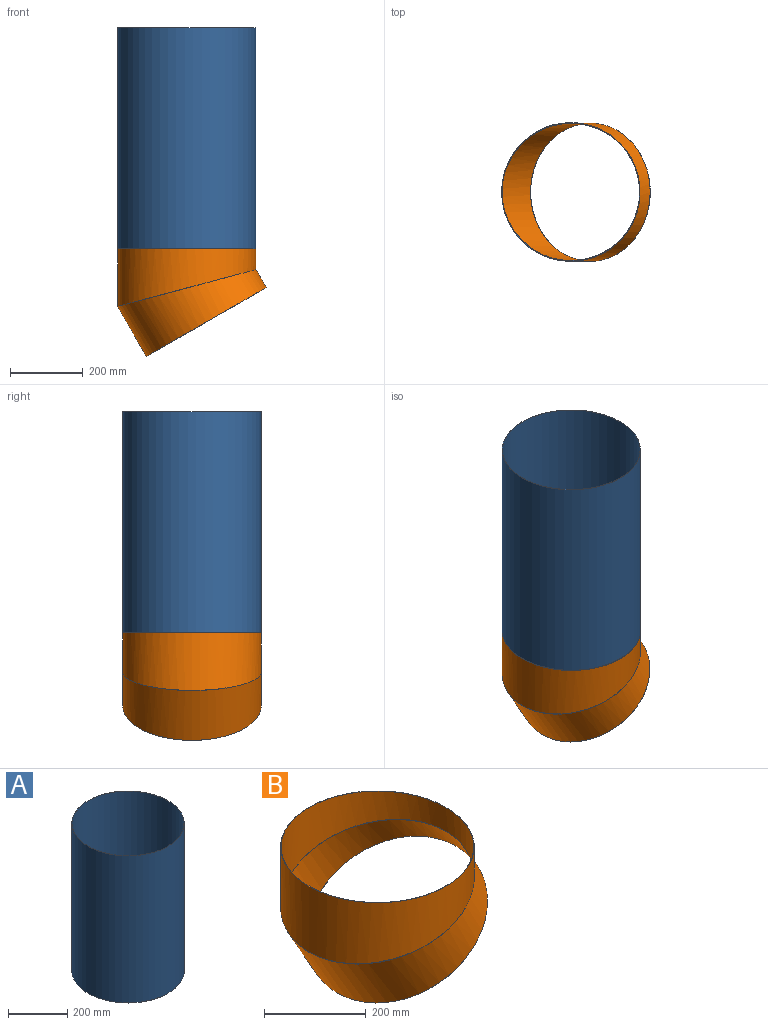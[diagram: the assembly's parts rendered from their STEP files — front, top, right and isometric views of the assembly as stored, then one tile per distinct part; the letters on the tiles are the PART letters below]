
ASSEMBLY  parts=2 mates=1
PART A: 4 faces, bbox 381x381x609.6 mm
  f0: cylinder r=190.5mm len=609.6mm, axis (0,0,-1), area 729658.8mm2, adj f1,f2
  f1: plane 381x381mm, normal (0,0,1), area 980.2mm2, adj f0,f3
  f2: plane 381x381mm, normal (0,0,-1), area 980.2mm2, adj f0,f3
  f3: cylinder r=189.68mm len=609.6mm, axis (0,0,-1), area 726515.4mm2, adj f1,f2
PART B: 6 faces, bbox 409.5x381x327.4 mm
  f0: plane 381x330.41mm, normal (0.5,0,-0.87), area 980.2mm2, adj f2,f4
  f1: plane 381x381mm, normal (0,0,1), area 980.2mm2, adj f3,f5
  f2: cylinder r=190.5mm len=409.47mm, axis (0.5,0,-0.87), area 129211.3mm2, adj f0,f3
  f3: cylinder r=190.5mm len=381mm, axis (0,0,-1), area 129211.3mm2, adj f1,f2
  f4: cylinder r=189.68mm len=408.01mm, axis (0.5,0,-0.87), area 128652.9mm2, adj f0,f5
  f5: cylinder r=189.68mm len=379.36mm, axis (0,0,-1), area 128652.9mm2, adj f1,f4
PLACE A t=(-69.77,-108.63,-430.96)mm
PLACE B t=(-69.77,-108.63,-430.96)mm
MATE fastened A.f0 <-> B.f3  axis (0,0,-1) through (-69.77,-108.63,-430.96)mm
